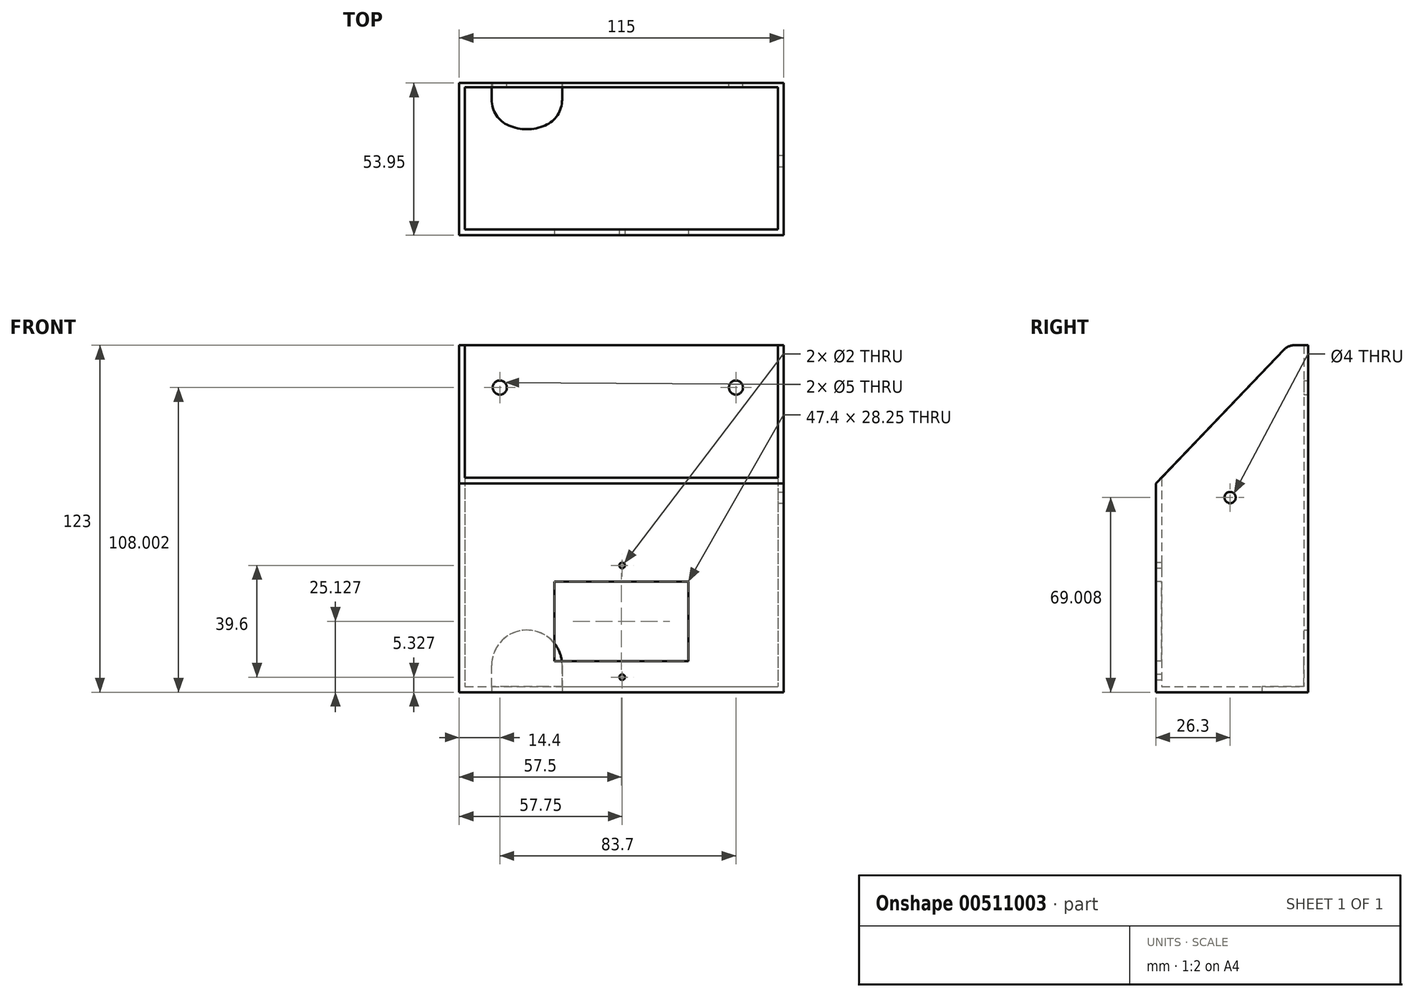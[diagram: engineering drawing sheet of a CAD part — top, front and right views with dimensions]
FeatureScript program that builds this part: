
annotation { "Feature Type Name" : "Feature", "Feature Type Description" : "" }
export const myFeature = defineFeature(function(context is Context, id is Id, definition is map)
    precondition{}
    {
        {
            var Q0;
            Q0=qCreatedBy(makeId("Right.planeOp"),FACE);
            var sketch = newSketch(context, id + "F0", { "sketchPlane" : qUnion([Q0])});
            skLineSegment(sketch, "E0.bottom", {"start": v(-46.95, -64.34) * mm, "end": v(7, -64.34) * mm});
            skLineSegment(sketch, "E0.left", {"start": v(-46.95, -64.34) * mm, "end": v(-46.95, 9.61) * mm});
            skLineSegment(sketch, "E0.right", {"start": v(7, -64.34) * mm, "end": v(7, 30.96) * mm});
            skLineSegment(sketch, "E1", {"start": v(7, 30.96) * mm, "end": v(7, 58.66) * mm});
            skLineSegment(sketch, "E2", {"start": v(7, 58.66) * mm, "end": v(0, 58.66) * mm});
            skLineSegment(sketch, "E3", {"start": v(0, 58.66) * mm, "end": v(-46.95, 9.61) * mm});
            skSolve(sketch);
        }
        {
            var Q0;
            Q0 = qSketchRegion(id + "F0", true);
            extrude(context, id + "F1", {"entities" : qUnion([Q0]), "depth" : (111 + 4) * mm});
        }
        {
            var Q0;
            Q0=makeQuery(id+"F1.opExtrude","SWEPT_FACE",FACE,{"disambiguationData":[OSD([sQuery(id+"F0.wireOp",EDGE,"E0.bottom")])]});
            var sketch = newSketch(context, id + "F2", { "sketchPlane" : qUnion([Q0])});
            skLineSegment(sketch, "E4.bottom", {"start": v(2, 44.95) * mm, "end": v(113, 44.95) * mm});
            skLineSegment(sketch, "E4.top", {"start": v(2, -5.5) * mm, "end": v(113, -5.5) * mm});
            skLineSegment(sketch, "E4.left", {"start": v(2, 44.95) * mm, "end": v(2, -5.5) * mm});
            skLineSegment(sketch, "E4.right", {"start": v(113, 44.95) * mm, "end": v(113, -5.5) * mm});
            skSolve(sketch);
        }
        {
            var Q0;
            Q0 = qSketchRegion(id + "F2", true);
            extrude(context, id + "F3", {"entities" : qUnion([Q0]), "operationType" : NewBodyOperationType.REMOVE, "oppositeDirection" : true, "depth" : 175.4 * mm, "hasSecondDirection" : true, "secondDirectionOppositeDirection" : true, "secondDirectionDepth" : 2 * mm});
        }
        {
            var Q0;
            Q0=makeQuery(id+"F1.opExtrude","SWEPT_FACE",FACE,{"disambiguationData":[OSD([sQuery(id+"F0.wireOp",EDGE,"E0.left")])]});
            var sketch = newSketch(context, id + "F4", { "sketchPlane" : qUnion([Q0])});
            skLineSegment(sketch, "E5.bottom", {"start": v(33.8, -25.09) * mm, "end": v(81.2, -25.09) * mm});
            skLineSegment(sketch, "E5.top", {"start": v(33.8, -53.34) * mm, "end": v(81.2, -53.34) * mm});
            skLineSegment(sketch, "E5.left", {"start": v(33.8, -25.09) * mm, "end": v(33.8, -53.34) * mm});
            skLineSegment(sketch, "E5.right", {"start": v(81.2, -25.09) * mm, "end": v(81.2, -53.34) * mm});
            skCircle(sketch, "E6", {"center": v(57.75, -19.41) * mm, "radius": 1 * mm});
            skCircle(sketch, "E7", {"center": v(57.75, -59.01) * mm, "radius": 1 * mm});
            skSolve(sketch);
        }
        {
            var Q0;
            Q0 = qSketchRegion(id + "F4", true);
            extrude(context, id + "F5", {"entities" : qUnion([Q0]), "operationType" : NewBodyOperationType.REMOVE, "oppositeDirection" : true, "depth" : 25 * mm});
        }
        {
            var Q0;
            Q0=makeQuery(id+"F1.opExtrude","SWEPT_FACE",FACE,{"disambiguationData":[OSD([sQuery(id+"F0.wireOp",EDGE,"E0.right"),sQuery(id+"F0.wireOp",EDGE,"E1")])]});
            var sketch = newSketch(context, id + "F6", { "sketchPlane" : qUnion([Q0])});
            skLineSegment(sketch, "E8.bottom", {"start": v(-36.5, -62.34) * mm, "end": v(-11.5, -62.34) * mm});
            skLineSegment(sketch, "E8.left", {"start": v(-36.5, -62.34) * mm, "end": v(-36.5, -54.84) * mm});
            skLineSegment(sketch, "E8.right", {"start": v(-11.5, -62.34) * mm, "end": v(-11.5, -54.84) * mm});
            skArc(sketch, "E9", {"start": v(-11.5, -54.84) * mm, "mid": v(-24, -42.34) * mm, "end": v(-36.5, -54.84) * mm});
            skSolve(sketch);
        }
        {
            var Q0;
            Q0 = qSketchRegion(id + "F6", true);
            extrude(context, id + "F7", {"entities" : qUnion([Q0]), "operationType" : NewBodyOperationType.REMOVE, "oppositeDirection" : true, "depth" : 2 * mm});
        }
        {
            var Q0;
            Q0=makeQuery(id+"F1.opExtrude","SWEPT_FACE",FACE,{"disambiguationData":[OSD([sQuery(id+"F0.wireOp",EDGE,"E0.right"),sQuery(id+"F0.wireOp",EDGE,"E1")])]});
            var sketch = newSketch(context, id + "F8", { "sketchPlane" : qUnion([Q0])});
            skCircle(sketch, "E10", {"center": v(-98.1, 43.66) * mm, "radius": 2.5 * mm});
            skCircle(sketch, "E11", {"center": v(-14.4, 43.66) * mm, "radius": 2.5 * mm});
            skSolve(sketch);
        }
        {
            var Q0;
            Q0 = qSketchRegion(id + "F8", true);
            extrude(context, id + "F9", {"entities" : qUnion([Q0]), "operationType" : NewBodyOperationType.REMOVE, "oppositeDirection" : true, "depth" : 5.7 * mm});
        }
        {
            var Q0;
            Q0=makeQuery(id+"F1.opExtrude","CAP_FACE",FACE,{"disambiguationData":[OSD([sQuery(id+"F0.wireOp",EDGE,"E0.bottom"),sQuery(id+"F0.wireOp",EDGE,"E0.left"),sQuery(id+"F0.wireOp",EDGE,"E0.right"),sQuery(id+"F0.wireOp",EDGE,"E1"),sQuery(id+"F0.wireOp",EDGE,"E2"),sQuery(id+"F0.wireOp",EDGE,"E3")])],"isStart":false});
            var sketch = newSketch(context, id + "F10", { "sketchPlane" : qUnion([Q0])});
            skCircle(sketch, "E12", {"center": v(-20.65, 4.67) * mm, "radius": 2 * mm});
            skPoint(sketch, "E13", {"position": v(6.25, 43.67) * mm});
            skSolve(sketch);
        }
        {
            var Q0;
            Q0 = qSketchRegion(id + "F10", true);
            extrude(context, id + "F11", {"entities" : qUnion([Q0]), "operationType" : NewBodyOperationType.REMOVE, "oppositeDirection" : true, "depth" : 25 * mm});
        }
        {
            var Q0;
            {var subQ0=sQuery(id+"F0.wireOp",EDGE,"E3");var subQ1=sQuery(id+"F0.wireOp",EDGE,"E2");Q0=makeQuery(id+"F3.boolean.opBoolean","SPLIT",EDGE,{"disambiguationData":[TD([makeQuery(id+"F3.opExtrude","SWEPT_FACE",FACE,{"disambiguationData":[OSD([sQuery(id+"F2.wireOp",EDGE,"E4.left")])]})])],"derivedFrom":makeQuery(id+"F1.opExtrude","SWEPT_EDGE",EDGE,{"disambiguationData":[OSD([subQ1,subQ0])]})});}
            var Q1;
            {var subQ0=sQuery(id+"F0.wireOp",EDGE,"E3");var subQ1=sQuery(id+"F0.wireOp",EDGE,"E2");Q1=makeQuery(id+"F3.boolean.opBoolean","SPLIT",EDGE,{"disambiguationData":[TD([makeQuery(id+"F3.opExtrude","SWEPT_FACE",FACE,{"disambiguationData":[OSD([sQuery(id+"F2.wireOp",EDGE,"E4.right")])]})])],"derivedFrom":makeQuery(id+"F1.opExtrude","SWEPT_EDGE",EDGE,{"disambiguationData":[OSD([subQ1,subQ0])]})});}
            fillet(context, id + "F12", {"entities" : qUnion([Q0, Q1]), "radius" : 5 * mm, "tangentPropagation" : true, "allowEdgeOverflow" : false});
        }
        {
            var Q0;
            Q0=makeQuery(id+"F1.opExtrude","SWEPT_FACE",FACE,{"disambiguationData":[OSD([sQuery(id+"F0.wireOp",EDGE,"E0.bottom")])]});
            var sketch = newSketch(context, id + "F13", { "sketchPlane" : qUnion([Q0])});
            skLineSegment(sketch, "E14", {"start": v(11.5, -7) * mm, "end": v(11.5, 3.58) * mm});
            skLineSegment(sketch, "E15", {"start": v(36.5, -7) * mm, "end": v(36.5, 3.58) * mm});
            skArc(sketch, "E16", {"start": v(36.5, 3.58) * mm, "mid": v(24, 9.38) * mm, "end": v(11.5, 3.58) * mm});
            skLineSegment(sketch, "E17", {"start": v(11.5, -7) * mm, "end": v(36.5, -7) * mm});
            skSolve(sketch);
        }
        {
            var Q0;
            Q0 = qSketchRegion(id + "F13", true);
            extrude(context, id + "F14", {"entities" : qUnion([Q0]), "operationType" : NewBodyOperationType.REMOVE, "oppositeDirection" : true, "depth" : 8.7 * mm, "offsetDistance" : 25 * mm});
        }
        {
            var Q0;
            Q0=makeQuery(id+"F14.boolean.opBoolean","COPY",EDGE,{"derivedFrom":makeQuery(id+"F14.opExtrude","SWEPT_EDGE",EDGE,{"disambiguationData":[OSD([sQuery(id+"F13.wireOp",EDGE,"E15"),sQuery(id+"F13.wireOp",EDGE,"E16")])]})});
            var Q1;
            Q1=makeQuery(id+"F14.boolean.opBoolean","COPY",EDGE,{"derivedFrom":makeQuery(id+"F14.opExtrude","SWEPT_EDGE",EDGE,{"disambiguationData":[OSD([sQuery(id+"F13.wireOp",EDGE,"E14"),sQuery(id+"F13.wireOp",EDGE,"E16")])]})});
            fillet(context, id + "F15", {"entities" : qUnion([Q0, Q1]), "radius" : 10 * mm, "tangentPropagation" : true, "allowEdgeOverflow" : false});
        }
    });
